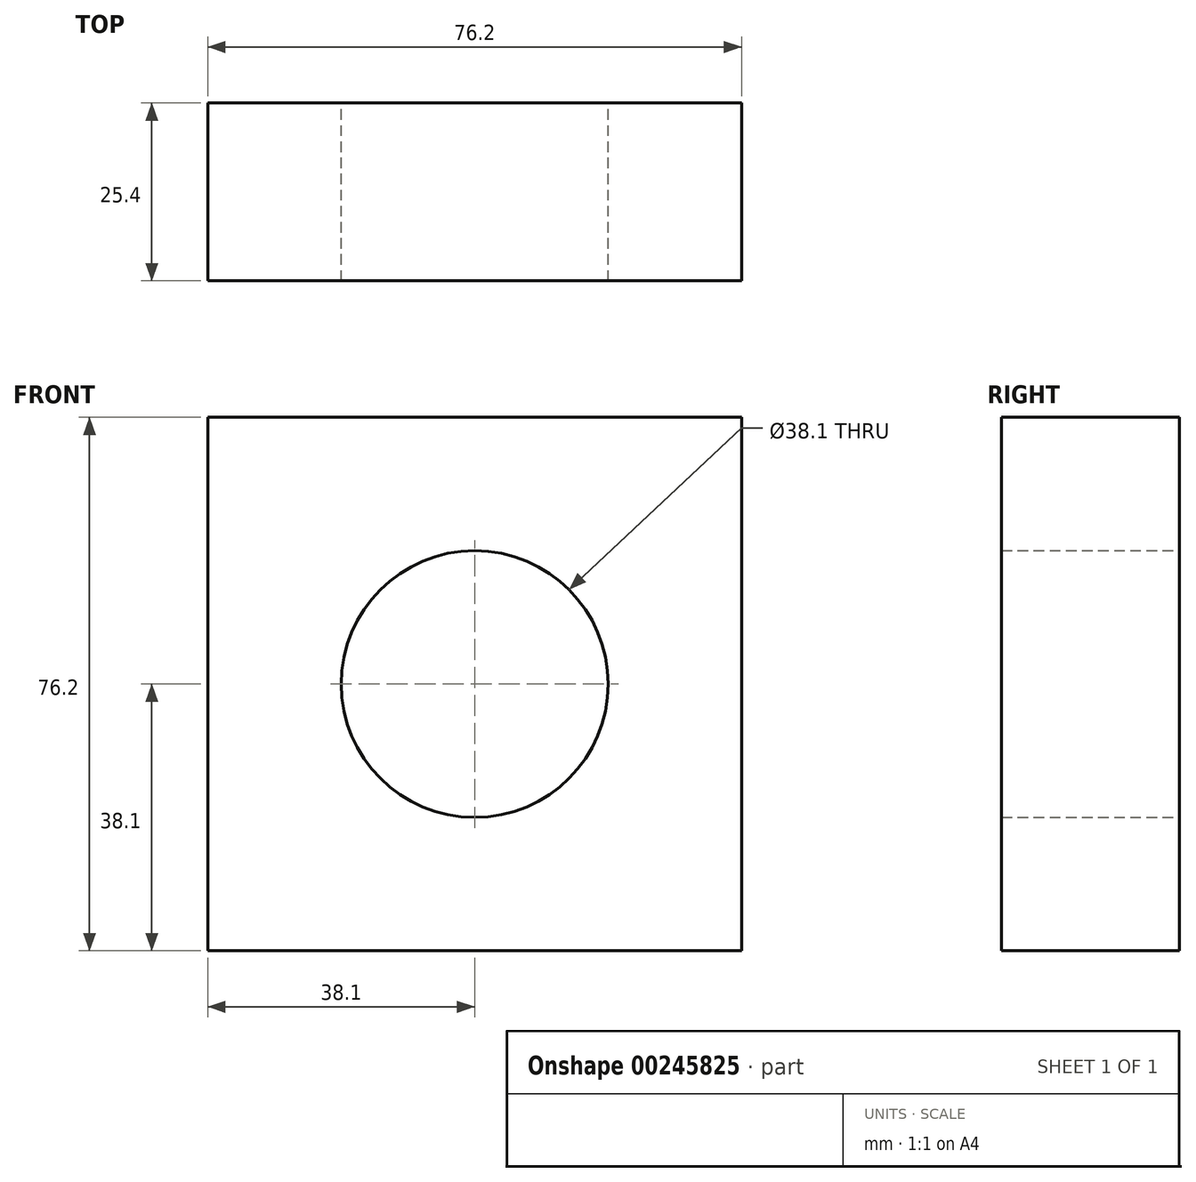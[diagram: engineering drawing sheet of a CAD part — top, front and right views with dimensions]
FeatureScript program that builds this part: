
annotation { "Feature Type Name" : "Feature", "Feature Type Description" : "" }
export const myFeature = defineFeature(function(context is Context, id is Id, definition is map)
    precondition{}
    {
        {
            var Q0;
            Q0=qCreatedBy(makeId("Front.planeOp"),FACE);
            var sketch = newSketch(context, id + "F0", { "sketchPlane" : qUnion([Q0])});
            skLineSegment(sketch, "E0.bottom", {"start": v(38.1, 38.1) * mm, "end": v(-38.1, 38.1) * mm});
            skLineSegment(sketch, "E0.top", {"start": v(38.1, -38.1) * mm, "end": v(-38.1, -38.1) * mm});
            skLineSegment(sketch, "E0.left", {"start": v(38.1, 38.1) * mm, "end": v(38.1, -38.1) * mm});
            skLineSegment(sketch, "E0.right", {"start": v(-38.1, 38.1) * mm, "end": v(-38.1, -38.1) * mm});
            skPoint(sketch, "E0.middle", {"position": v(0, 0) * mm});
            skCircle(sketch, "E1", {"center": v(0, 0) * mm, "radius": 19.05 * mm});
            skCircle(sketch, "E2", {"center": v(0, 0) * mm, "radius": 5.3 * mm});
            skSolve(sketch);
        }
        {
            var Q0;
            Q0=makeQuery(id+"F0.imprint","IMPRINT",FACE,{"disambiguationData":[TD([[makeQuery(id+"F0.imprint","IMPRINT",EDGE,{"derivedFrom":sQuery(id+"F0.wireOp",EDGE,"E0.bottom")}),1.0]])]});
            extrude(context, id + "F1", {"entities" : qUnion([Q0]), "depth" : 25.4 * mm});
        }
        {
            var Q0;
            Q0=sQuery(id+"F0.wireOp",EDGE,"E1");
            extrude(context, id + "F2", {"bodyType" : ToolBodyType.SURFACE, "operationType" : NewBodyOperationType.ADD, "surfaceEntities" : qUnion([Q0]), "depth" : 25.4 * mm, "hasSecondDirection" : true, "secondDirectionOppositeDirection" : true, "secondDirectionDepth" : 25.4 * mm});
        }
        {
            var Q0;
            Q0=sQuery(id+"F0.wireOp",EDGE,"E1");
            extrude(context, id + "F3", {"bodyType" : ToolBodyType.SURFACE, "surfaceEntities" : qUnion([Q0]), "endBound" : BoundingType.SYMMETRIC, "depth" : 63.5 * mm});
        }
    });
